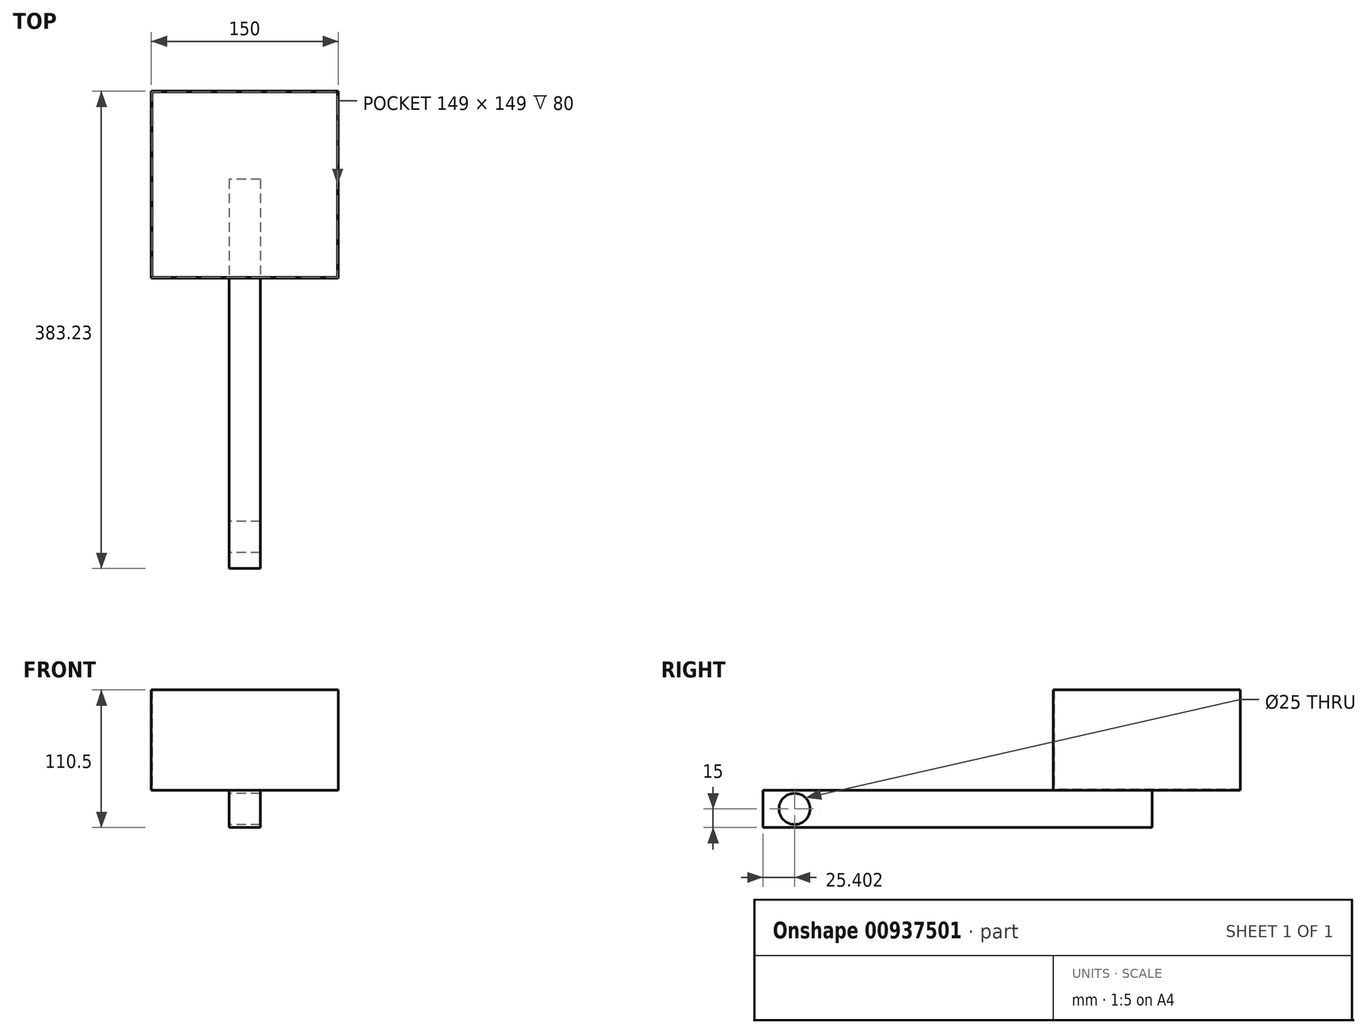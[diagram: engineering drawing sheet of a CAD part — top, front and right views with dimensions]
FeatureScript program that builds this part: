
annotation { "Feature Type Name" : "Feature", "Feature Type Description" : "" }
export const myFeature = defineFeature(function(context is Context, id is Id, definition is map)
    precondition{}
    {
        {
            var Q0;
            Q0=qCreatedBy(makeId("Top.planeOp"),FACE);
            var sketch = newSketch(context, id + "F0", { "sketchPlane" : qUnion([Q0])});
            skLineSegment(sketch, "E0.bottom", {"start": v(-61.89, 138.43) * mm, "end": v(88.11, 138.43) * mm});
            skLineSegment(sketch, "E0.top", {"start": v(-61.89, 137.93) * mm, "end": v(88.11, 137.93) * mm});
            skLineSegment(sketch, "E0.left", {"start": v(-61.89, 138.43) * mm, "end": v(-61.89, 137.93) * mm});
            skLineSegment(sketch, "E0.right", {"start": v(88.11, 138.43) * mm, "end": v(88.11, 137.93) * mm});
            skLineSegment(sketch, "E1.bottom", {"start": v(88.11, 137.93) * mm, "end": v(87.61, 137.93) * mm});
            skLineSegment(sketch, "E1.top", {"start": v(88.11, -11.07) * mm, "end": v(87.61, -11.07) * mm});
            skLineSegment(sketch, "E1.left", {"start": v(88.11, 137.93) * mm, "end": v(88.11, -11.07) * mm});
            skLineSegment(sketch, "E1.right", {"start": v(87.61, 137.93) * mm, "end": v(87.61, -11.07) * mm});
            skLineSegment(sketch, "E2.bottom", {"start": v(88.11, -11.07) * mm, "end": v(-61.89, -11.07) * mm});
            skLineSegment(sketch, "E2.top", {"start": v(88.11, -11.57) * mm, "end": v(-61.89, -11.57) * mm});
            skLineSegment(sketch, "E2.left", {"start": v(88.11, -11.07) * mm, "end": v(88.11, -11.57) * mm});
            skLineSegment(sketch, "E2.right", {"start": v(-61.89, -11.07) * mm, "end": v(-61.89, -11.57) * mm});
            skLineSegment(sketch, "E3.bottom", {"start": v(-61.89, 137.93) * mm, "end": v(-61.39, 137.93) * mm});
            skLineSegment(sketch, "E3.top", {"start": v(-61.89, -11.07) * mm, "end": v(-61.39, -11.07) * mm});
            skLineSegment(sketch, "E3.left", {"start": v(-61.89, 137.93) * mm, "end": v(-61.89, -11.07) * mm});
            skLineSegment(sketch, "E3.right", {"start": v(-61.39, 137.93) * mm, "end": v(-61.39, -11.07) * mm});
            skSolve(sketch);
        }
        {
            var Q0;
            Q0=makeQuery(id+"F0.imprint","IMPRINT",FACE,{"disambiguationData":[TD([[makeQuery(id+"F0.imprint","IMPRINT",EDGE,{"derivedFrom":sQuery(id+"F0.wireOp",EDGE,"E0.bottom")}),-1.0]])]});
            var Q1;
            {var subQ2=sQuery(id+"F0.wireOp",EDGE,"E3.left");Q1=makeQuery(id+"F0.imprint","IMPRINT",FACE,{"disambiguationData":[TD([[makeQuery(id+"F0.imprint","IMPRINT",EDGE,{"derivedFrom":subQ2}),1.0]])]});}
            var Q2;
            Q2=makeQuery(id+"F0.imprint","IMPRINT",FACE,{"disambiguationData":[TD([[makeQuery(id+"F0.imprint","IMPRINT",EDGE,{"derivedFrom":sQuery(id+"F0.wireOp",EDGE,"E1.top")}),-1.0]])]});
            var Q3;
            {var subQ3=sQuery(id+"F0.wireOp",EDGE,"E1.top");Q3=makeQuery(id+"F0.imprint","IMPRINT",FACE,{"disambiguationData":[TD([[makeQuery(id+"F0.imprint","IMPRINT",EDGE,{"derivedFrom":subQ3}),1.0]])]});}
            extrude(context, id + "F1", {"entities" : qUnion([Q0, Q1, Q2, Q3]), "depth" : 80 * mm, "offsetDistance" : 25.4 * mm});
        }
        {
            var Q0;
            Q0=makeQuery(id+"F1.opExtrude","CAP_FACE",FACE,{"disambiguationData":[OSD([sQuery(id+"F0.wireOp",EDGE,"E0.bottom"),sQuery(id+"F0.wireOp",EDGE,"E0.top"),sQuery(id+"F0.wireOp",EDGE,"E0.left"),sQuery(id+"F0.wireOp",EDGE,"E0.right"),sQuery(id+"F0.wireOp",EDGE,"E1.left"),sQuery(id+"F0.wireOp",EDGE,"E1.right"),sQuery(id+"F0.wireOp",EDGE,"E2.bottom"),sQuery(id+"F0.wireOp",EDGE,"E2.top"),sQuery(id+"F0.wireOp",EDGE,"E2.left"),sQuery(id+"F0.wireOp",EDGE,"E2.right"),sQuery(id+"F0.wireOp",EDGE,"E3.left"),sQuery(id+"F0.wireOp",EDGE,"E3.right")])],"isStart":true});
            var sketch = newSketch(context, id + "F2", { "sketchPlane" : qUnion([Q0])});
            skLineSegment(sketch, "E4.bottom", {"start": v(88.11, -138.43) * mm, "end": v(-61.89, -138.43) * mm});
            skLineSegment(sketch, "E4.top", {"start": v(88.11, 11.57) * mm, "end": v(-61.89, 11.57) * mm});
            skLineSegment(sketch, "E4.left", {"start": v(88.11, -138.43) * mm, "end": v(88.11, 11.57) * mm});
            skLineSegment(sketch, "E4.right", {"start": v(-61.89, -138.43) * mm, "end": v(-61.89, 11.57) * mm});
            skSolve(sketch);
        }
        {
            var Q0;
            Q0 = qSketchRegion(id + "F2", true);
            extrude(context, id + "F3", {"entities" : qUnion([Q0]), "operationType" : NewBodyOperationType.ADD, "depth" : 0.5 * mm, "offsetDistance" : 25.4 * mm});
        }
        {
            var Q0;
            Q0=makeQuery(id+"F3.opExtrude","CAP_FACE",FACE,{"disambiguationData":[OSD([sQuery(id+"F2.wireOp",EDGE,"E4.bottom"),sQuery(id+"F2.wireOp",EDGE,"E4.top"),sQuery(id+"F2.wireOp",EDGE,"E4.left"),sQuery(id+"F2.wireOp",EDGE,"E4.right")])],"isStart":false});
            var sketch = newSketch(context, id + "F4", { "sketchPlane" : qUnion([Q0])});
            skLineSegment(sketch, "E5.bottom", {"start": v(25.61, -67.63) * mm, "end": v(0.61, -67.63) * mm});
            skLineSegment(sketch, "E5.top", {"start": v(25.61, 244.8) * mm, "end": v(0.61, 244.8) * mm});
            skLineSegment(sketch, "E5.left", {"start": v(25.61, -67.63) * mm, "end": v(25.61, 244.8) * mm});
            skLineSegment(sketch, "E5.right", {"start": v(0.61, -67.63) * mm, "end": v(0.61, 244.8) * mm});
            skLineSegment(sketch, "E6", {"start": v(0.61, 11.57) * mm, "end": v(-61.89, 11.57) * mm});
            skLineSegment(sketch, "E7", {"start": v(25.61, 11.57) * mm, "end": v(88.11, 11.57) * mm});
            skSolve(sketch);
        }
        {
            var Q0;
            Q0 = qSketchRegion(id + "F4", true);
            extrude(context, id + "F5", {"entities" : qUnion([Q0]), "operationType" : NewBodyOperationType.ADD, "depth" : 30 * mm, "offsetDistance" : 25.4 * mm});
        }
        {
            var Q0;
            Q0=makeQuery(id+"F5.opExtrude","SWEPT_FACE",FACE,{"disambiguationData":[OSD([sQuery(id+"F4.wireOp",EDGE,"E5.left")])]});
            var sketch = newSketch(context, id + "F6", { "sketchPlane" : qUnion([Q0])});
            skLineSegment(sketch, "E8", {"start": v(85.95, -0.5) * mm, "end": v(85.95, -30.5) * mm});
            skCircle(sketch, "E9", {"center": v(85.95, -15.5) * mm, "radius": 1.08 * mm});
            skSolve(sketch);
        }
        {
            var Q0;
            {var subQ0=sQuery(id+"F6.wireOp",EDGE,"E9");var subQ1=sQuery(id+"F6.wireOp",EDGE,"E8");var subQ2=makeQuery(id+"F6.imprint","INTERSECT",VERTEX,{"disambiguationData":[OD(0.0)],"derivedFrom":[subQ1,subQ0]});Q0=makeQuery(id+"F6.imprint","IMPRINT",FACE,{"disambiguationData":[TD([[makeQuery(id+"F6.imprint","IMPRINT",EDGE,{"disambiguationData":[TD([[subQ2,-1.0]])],"derivedFrom":subQ1}),-1.0]])]});}
            var Q1;
            {var subQ0=sQuery(id+"F6.wireOp",EDGE,"E9");var subQ1=sQuery(id+"F6.wireOp",EDGE,"E8");var subQ2=makeQuery(id+"F6.imprint","INTERSECT",VERTEX,{"disambiguationData":[OD(0.0)],"derivedFrom":[subQ1,subQ0]});Q1=makeQuery(id+"F6.imprint","IMPRINT",FACE,{"disambiguationData":[TD([[makeQuery(id+"F6.imprint","IMPRINT",EDGE,{"disambiguationData":[TD([[subQ2,-1.0]])],"derivedFrom":subQ1}),1.0]])]});}
            extrude(context, id + "F7", {"entities" : qUnion([Q0, Q1]), "operationType" : NewBodyOperationType.REMOVE, "endBound" : BoundingType.THROUGH_ALL, "oppositeDirection" : true, "depth" : 25.4 * mm, "offsetDistance" : 25.4 * mm});
        }
        {
            var Q0;
            Q0=makeQuery(id+"F5.opExtrude","SWEPT_FACE",FACE,{"disambiguationData":[OSD([sQuery(id+"F4.wireOp",EDGE,"E5.right")])]});
            var sketch = newSketch(context, id + "F8", { "sketchPlane" : qUnion([Q0])});
            skLineSegment(sketch, "E10", {"start": v(219.4, -0.5) * mm, "end": v(219.4, -30.5) * mm});
            skCircle(sketch, "E11", {"center": v(219.4, -15.5) * mm, "radius": 12.5 * mm});
            skSolve(sketch);
        }
        {
            var Q0;
            {var subQ0=sQuery(id+"F8.wireOp",EDGE,"E11");var subQ1=sQuery(id+"F8.wireOp",EDGE,"E10");var subQ2=makeQuery(id+"F8.imprint","INTERSECT",VERTEX,{"disambiguationData":[OD(0.0)],"derivedFrom":[subQ1,subQ0]});Q0=makeQuery(id+"F8.imprint","IMPRINT",FACE,{"disambiguationData":[TD([[makeQuery(id+"F8.imprint","IMPRINT",EDGE,{"disambiguationData":[TD([[subQ2,-1.0]])],"derivedFrom":subQ1}),1.0]])]});}
            var Q1;
            {var subQ0=sQuery(id+"F8.wireOp",EDGE,"E11");var subQ1=sQuery(id+"F8.wireOp",EDGE,"E10");var subQ2=makeQuery(id+"F8.imprint","INTERSECT",VERTEX,{"disambiguationData":[OD(0.0)],"derivedFrom":[subQ1,subQ0]});Q1=makeQuery(id+"F8.imprint","IMPRINT",FACE,{"disambiguationData":[TD([[makeQuery(id+"F8.imprint","IMPRINT",EDGE,{"disambiguationData":[TD([[subQ2,-1.0]])],"derivedFrom":subQ1}),-1.0]])]});}
            extrude(context, id + "F9", {"entities" : qUnion([Q0, Q1]), "operationType" : NewBodyOperationType.REMOVE, "endBound" : BoundingType.THROUGH_ALL, "oppositeDirection" : true, "depth" : 25 * mm, "offsetDistance" : 25 * mm});
        }
    });
